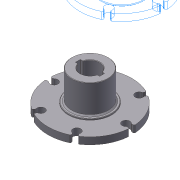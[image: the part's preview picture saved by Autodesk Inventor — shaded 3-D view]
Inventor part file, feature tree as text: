
AUTODESK INVENTOR PART (.ipt)
format: ipt  version: 2012 (Build 160160000, 160)  size: 192,512 bytes
history: native  units: in
note: dims shown in document units (in); Inventor stores cm internally (conversion verified against a paired STEP export)
features: chamfer x1, other x1, imported_body x1
ambient origin geometry x8: Origin, YZ Plane, XZ Plane, XY Plane, X Axis, Y Axis, Z Axis, Center Point
feature tree (3):
  chamfer  "Chamfer3"  [1 undecoded]
  other  "500EX-Key-Hub1"
  imported_body  "Base1"
note: 1 required parameter value undecoded (feature->parameter linkage not recoverable at this tier; creation-order binding heuristic only, values carry confidence <= 0.55)
